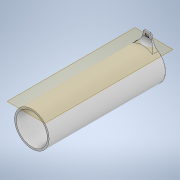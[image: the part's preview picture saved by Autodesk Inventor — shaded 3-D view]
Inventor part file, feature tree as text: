
AUTODESK INVENTOR PART (.ipt)
format: ipt  version: 2021 (Build 250183000, 183)  size: 723,456 bytes
history: native  units: in
note: dims shown in document units (in); Inventor stores cm internally (conversion verified against a paired STEP export)
features: sketch x7, extrude x6, projected_geometry x6, fillet x5, pattern_linear x2, hole x1, plane x1
ambient origin geometry x8: Origin, YZ Plane, XZ Plane, XY Plane, X Axis, Y Axis, Z Axis, Center Point
bodies: Solid1 (feature_tree)
feature tree (28):
  extrude  "Extrusion1"  Depth=5.9055in TaperAngle=0.0deg
  hole  "Hole1"  [1 undecoded]
  plane  "Work Plane1"
  extrude  "Extrusion2"  Depth=0.4724in TaperAngle=0.0deg
  fillet  "Fillet1"  Radius=0.0394in
  extrude  "Extrusion3"  Depth=0.0157in
  extrude  "Extrusion4"  Depth=0.0787in TaperAngle=0.0deg
  fillet  "Fillet2"  Radius=0.1929in
  fillet  "Fillet3"  Radius=0.122in
  fillet  "Fillet4"  Radius=0.1004in
  fillet  "Fillet5"  Radius=0.0984in
  extrude  "Extrusion5"  TaperAngle=0.0deg  [1 undecoded]
  pattern_linear  "Rectangular Pattern1"  Spacing1=0.0591in  [1 undecoded]
  extrude  "Extrusion6"  Depth=0.0394in
  pattern_linear  "Rectangular Pattern2"  Spacing1=0.7087in  [1 undecoded]
  sketch  "Sketch2"  dims[d2=1.752in d3=5.9055in d4=0.0in]
  sketch  "Sketch3"  dims[d5=1.378in]
  projected_geometry  "Projected Loop1"
  sketch  "Sketch4"  dims[d6=1.5748in d7=3.3in d8=0.3125in d9=0.164in d10=0.5635in d11=5.4134in d12=0.8108in d13=0.3937in]
  projected_geometry  "Projected Loop2"
  sketch  "Sketch5"  dims[d14=0.0551in d15=0.4724in d16=0.0in]
  projected_geometry  "Projected Loop3"
  projected_geometry  "Projected Loop4"
  sketch  "Sketch6"  dims[d17=0.0295in d18=0.0in d19=0.2362in d20=0.0394in]
  sketch  "Sketch7"  dims[d21=0.0157in d22=0.0157in]
  projected_geometry  "Projected Loop5"
  sketch  "Sketch8"  dims[d23=0.377in d24=0.0in d25=0.9697in d26=0.0in d27=0.1929in d28=0.122in d29=0.1004in d30=0.0984in d31=0.0in d32=0.0in d33=0.0591in d34=0.0394in d35=0.7087in d36=0.0217in d37=0.0157in d38=0.0157in d39=0.9395in d40=0.0in d41=2.7559in d43=0.0394in d44=2.7559in d46=0.1575in d47=0.0197in d48=1.9685in d49=0.0059in d50=0.0in d51=9.0551in d53=0.0787in]
  projected_geometry  "Projected Loop6"
note: 4 required parameter values undecoded (feature->parameter linkage not recoverable at this tier; creation-order binding heuristic only, values carry confidence <= 0.55)
